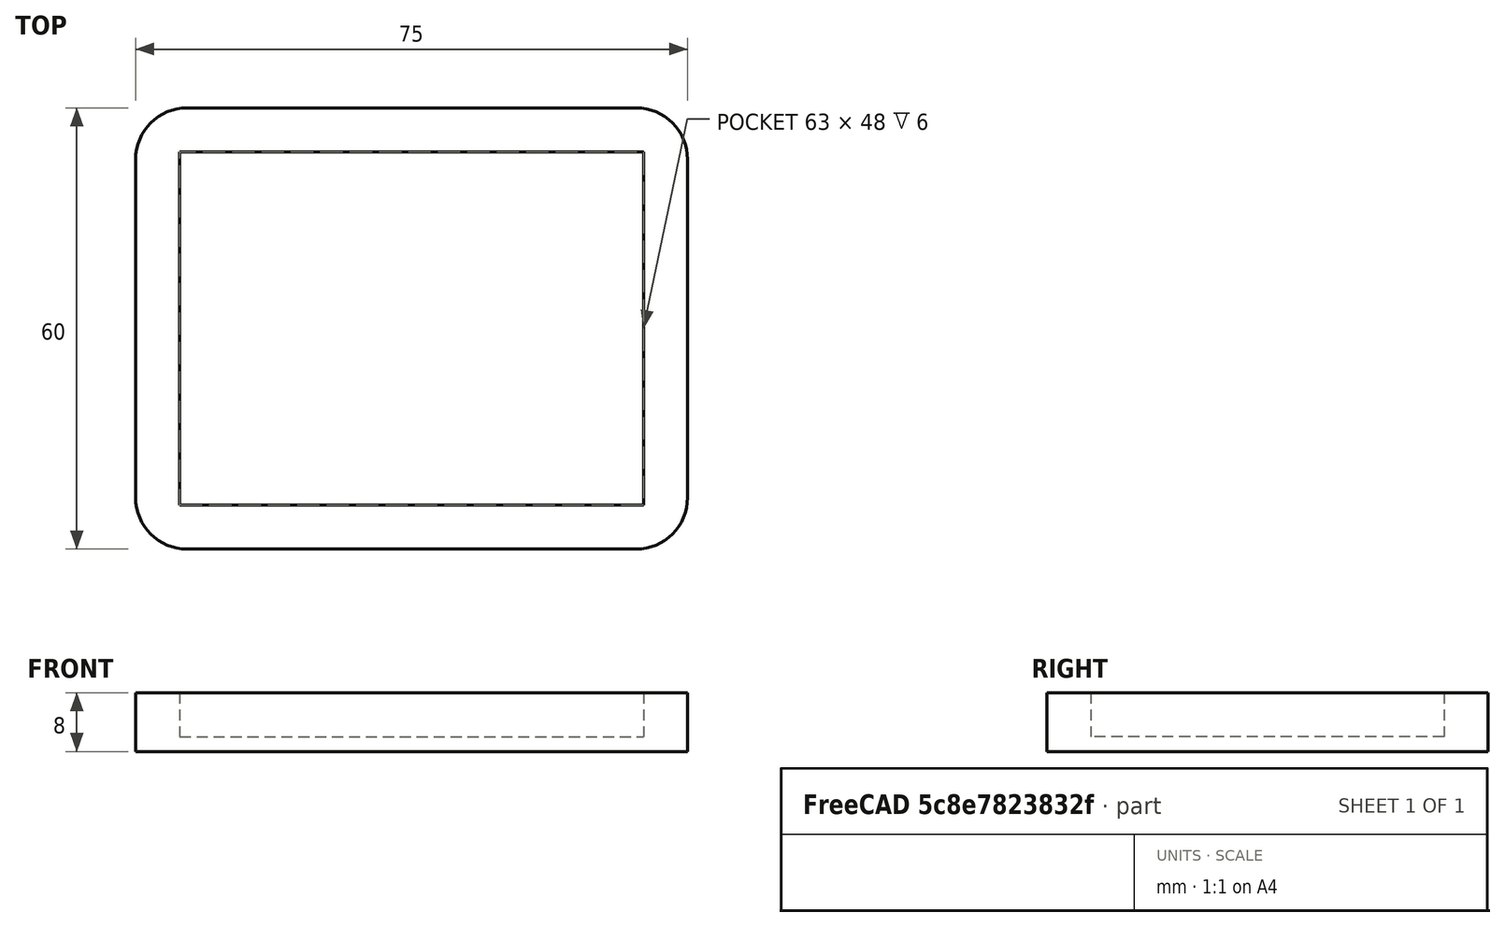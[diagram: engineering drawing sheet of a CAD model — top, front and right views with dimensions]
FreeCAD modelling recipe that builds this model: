
FCSTD DOCUMENT  (FreeCAD 0.18R4 (GitTag))
Label: Tischfuß rund
License: All rights reserved
LicenseURL: http://en.wikipedia.org/wiki/All_rights_reserved
objects: Sketcher::SketchObject×2, PartDesign::Pad×1, PartDesign::Pocket×1, PartDesign::Body×1, Mesh::Feature×1
note: 7 computed .brp shape members not serialized (recipe doc carries the construction recipe); baked Part::Feature solids carry a one-line shape summary decoded from their .brp

FEATURE [Sketcher::SketchObject] Sketch
  MapMode = 5
  Support = -> [XY_Plane]
  sketch-geometry (8):
    g0: LineSegment StartX=-33 StartY=20 StartZ=0 EndX=28 EndY=20 EndZ=0
    g1: LineSegment StartX=35 StartY=13 StartZ=0 EndX=35 EndY=-33 EndZ=0
    g2: LineSegment StartX=28 StartY=-40 StartZ=0 EndX=-33 EndY=-40 EndZ=0
    g3: LineSegment StartX=-40 StartY=-33 StartZ=0 EndX=-40 EndY=13 EndZ=0
    g4: ArcOfCircle CenterX=-33 CenterY=13 CenterZ=0 NormalX=0 NormalY=0 NormalZ=1 AngleXU=0 Radius=7 StartAngle=1.5708 EndAngle=3.14159
    g5: ArcOfCircle CenterX=28 CenterY=13 CenterZ=0 NormalX=0 NormalY=0 NormalZ=1 AngleXU=0 Radius=7 StartAngle=0 EndAngle=1.5708
    g6: ArcOfCircle CenterX=-33 CenterY=-33 CenterZ=0 NormalX=0 NormalY=0 NormalZ=1 AngleXU=0 Radius=7 StartAngle=3.14159 EndAngle=4.71239
    g7: ArcOfCircle CenterX=28 CenterY=-33 CenterZ=0 NormalX=0 NormalY=0 NormalZ=1 AngleXU=0 Radius=7 StartAngle=4.71239 EndAngle=6.28319
  constraints (20):
    c: Horizontal(g0)
    c: Horizontal(g2)
    c: Vertical(g1)
    c: Vertical(g3)
    c: Distance(g-1,g0) = 20
    c: Distance(g-1,g1) = 35
    c: Tangent(g0,g4) = 1.5708
    c: Tangent(g3,g4) = 1.5708
    c: Tangent(g0,g5) = 1.5708
    c: Tangent(g1,g5) = 1.5708
    c: Tangent(g2,g6) = 1.5708
    c: Tangent(g3,g6) = 1.5708
    c: Tangent(g1,g7) = 1.5708
    c: Tangent(g2,g7) = 1.5708
    c: Radius(g4) = 7
    c: Radius(g5) = 7
    c: Radius(g7) = 7
    c: Radius(g6) = 7
    c: DistanceY(g2,g0) = 60
    c: DistanceX(g3,g1) = 75
FEATURE [PartDesign::Pad] Pad
  Length = 8
  Length2 = 100
  Profile = -> Sketch
  Refine = true
  Type = 0
FEATURE [Sketcher::SketchObject] Sketch001
  MapMode = 5
  Placement = pos=(0,0,8) rot=(0,0,1;0rad)
  Support = -> [Pad]
  sketch-geometry (4):
    g0: LineSegment StartX=-34 StartY=14 StartZ=0 EndX=29 EndY=14 EndZ=0
    g1: LineSegment StartX=29 StartY=14 StartZ=0 EndX=29 EndY=-34 EndZ=0
    g2: LineSegment StartX=29 StartY=-34 StartZ=0 EndX=-34 EndY=-34 EndZ=0
    g3: LineSegment StartX=-34 StartY=-34 StartZ=0 EndX=-34 EndY=14 EndZ=0
  constraints (12):
    c: Coincident(g0,g1)
    c: Coincident(g1,g2)
    c: Coincident(g2,g3)
    c: Coincident(g3,g0)
    c: Horizontal(g0)
    c: Horizontal(g2)
    c: Vertical(g1)
    c: Vertical(g3)
    c: DistanceY(g1,g1) = 48
    c: DistanceX(g0,g0) = 63
    c: DistanceX(g-1,g0) = 29
    c: DistanceY(g-1,g0) = 14  '17'
FEATURE [PartDesign::Pocket] Pocket
  BaseFeature = -> Pad
  Length = 6
  Length2 = 100
  Profile = -> Sketch001
  Refine = true
  Type = 0
FEATURE [PartDesign::Body] Body
  Group = -> [Sketch,Pad,Sketch001,Pocket]
  Origin = -> Origin
  Tip = -> Pocket
FEATURE [Mesh::Feature] Mesh  label="Pocket (Meshed)"
